# Revit family: T1330
name_source: partatom
category: Plumbing Fixtures
revit_build: Autodesk Revit 2018 (Build: 20170223_1515(x64)
units: mm (PartAtom-declared; Revit-internal decimal feet)

## family parameters
Cut with Voids When Loaded = No
Host = Face
Part Type = Normal
Room Calculation Point = No
Round Connector Dimension = Use Diameter
Shared = No

## types (17) — shared parameters
Default Elevation = 48.00"
Description = 4” INTERNAL WIDTH, PRESLOPED, FABRICATED STEEL CHANNEL
Manufacturer = MIFAB
Material = Paint - Sherwin Williams Paint - #952C2A - Bellwood Red
URL = WWW.MIFAB.COM

## per-type parameters (varying)
| type | C1 (Shallow Invert) | Length |
| T1331 | 4.00" | 78.74" |
| T1331N | 4.78" | 78.74" |
| T1331N-BO3 | 4.78" | 78.74" |
| T1331N-BO4 | 4.78" | 78.74" |
| T1331N-1M | 4.78" | 39.34" |
| T1332 | 4.78" | 78.74" |
| T1333 | 5.56" | 78.74" |
| T1333N | 6.34" | 78.74" |
| T1333N-BO3 | 6.34" | 78.74" |
| T1333N-BO4 | 6.34" | 78.74" |
| T1333N-1M | 6.34" | 39.37" |
| T1334 | 6.34" | 78.74" |
| T1335 | 7.12" | 78.74" |
| T1335N | 7.90" | 78.74" |
| T1335N-BO3 | 7.90" | 78.74" |
| T1335N-BO4 | 7.90" | 78.74" |
| T1335N-1M | 7.90" | 39.37" |

note: column(s) folded — value = type name in every type: Model

## geometry (parser evidence)
native form markers: Sweep x2
no freeform markers — native parametric forms only
